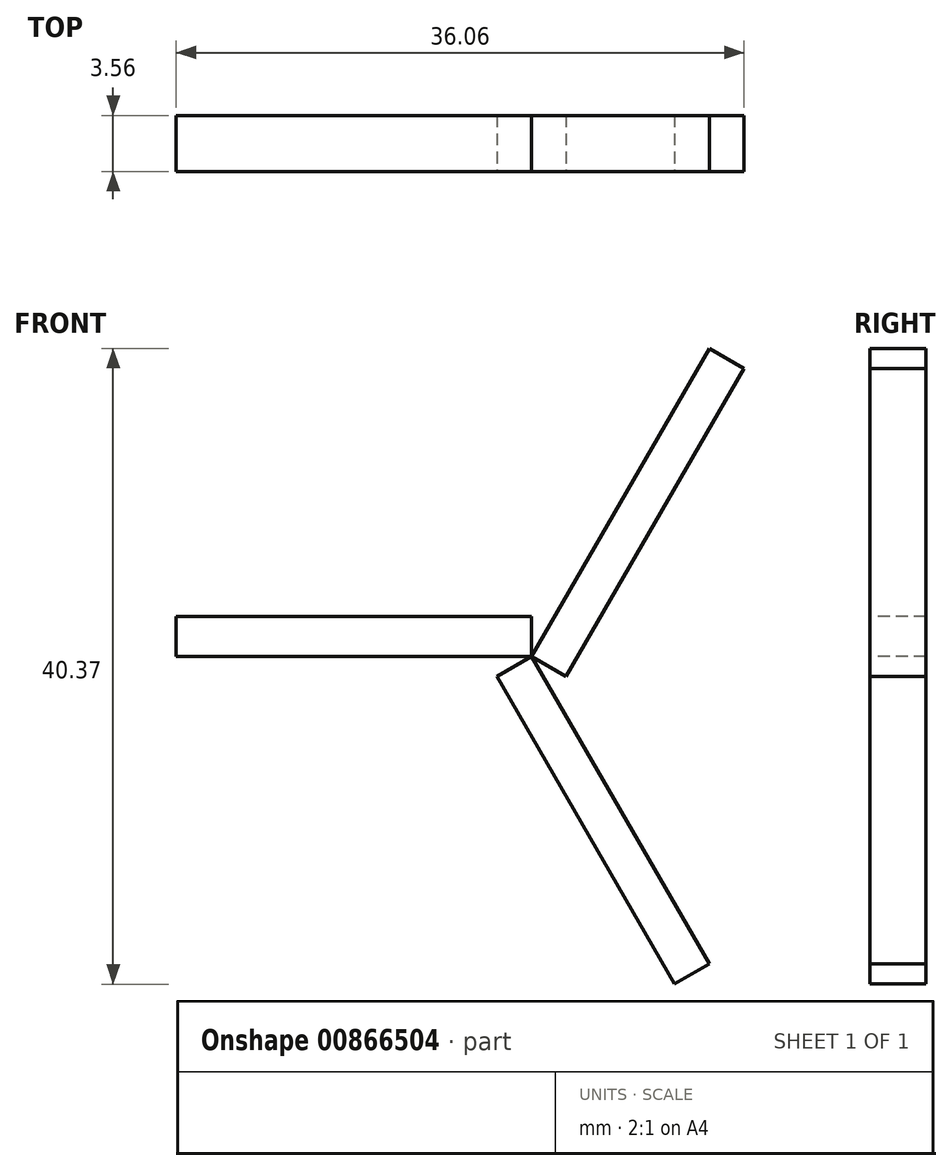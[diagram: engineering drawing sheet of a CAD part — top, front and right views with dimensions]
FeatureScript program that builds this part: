
annotation { "Feature Type Name" : "Feature", "Feature Type Description" : "" }
export const myFeature = defineFeature(function(context is Context, id is Id, definition is map)
    precondition{}
    {
        {
            var Q0;
            Q0=qCreatedBy(makeId("Top.planeOp"),FACE);
            var sketch = newSketch(context, id + "F0", { "sketchPlane" : qUnion([Q0])});
            skLineSegment(sketch, "E0.bottom", {"start": v(0, 1.78) * mm, "end": v(-22.57, 1.78) * mm});
            skLineSegment(sketch, "E0.top", {"start": v(0, -1.78) * mm, "end": v(-22.57, -1.78) * mm});
            skLineSegment(sketch, "E0.left", {"start": v(0, 1.78) * mm, "end": v(0, -1.78) * mm});
            skLineSegment(sketch, "E0.right", {"start": v(-22.57, 1.78) * mm, "end": v(-22.57, -1.78) * mm});
            skSolve(sketch);
        }
        {
            var Q0;
            Q0 = qSketchRegion(id + "F0", true);
            extrude(context, id + "F1", {"entities" : qUnion([Q0]), "depth" : 2.54 * mm, "offsetDistance" : 25.4 * mm});
        }
        {
            var Q0;
            Q0=makeQuery(id+"F1.opExtrude","SWEPT_BODY",BODY,{"disambiguationData":[OSD([sQuery(id+"F0.wireOp",EDGE,"E0.bottom"),sQuery(id+"F0.wireOp",EDGE,"E0.top"),sQuery(id+"F0.wireOp",EDGE,"E0.left"),sQuery(id+"F0.wireOp",EDGE,"E0.right")])]});
            var Q1;
            Q1=makeQuery(id+"F1.opExtrude","CAP_EDGE",EDGE,{"disambiguationData":[OSD([sQuery(id+"F0.wireOp",EDGE,"E0.left")])],"isStart":true});
            circularPattern(context, id + "F2", {"entities" : qUnion([Q0]), "axis" : qUnion([Q1]), "angle" : 360 * degree, "instanceCount" : 3, "equalSpace" : true});
        }
    });
